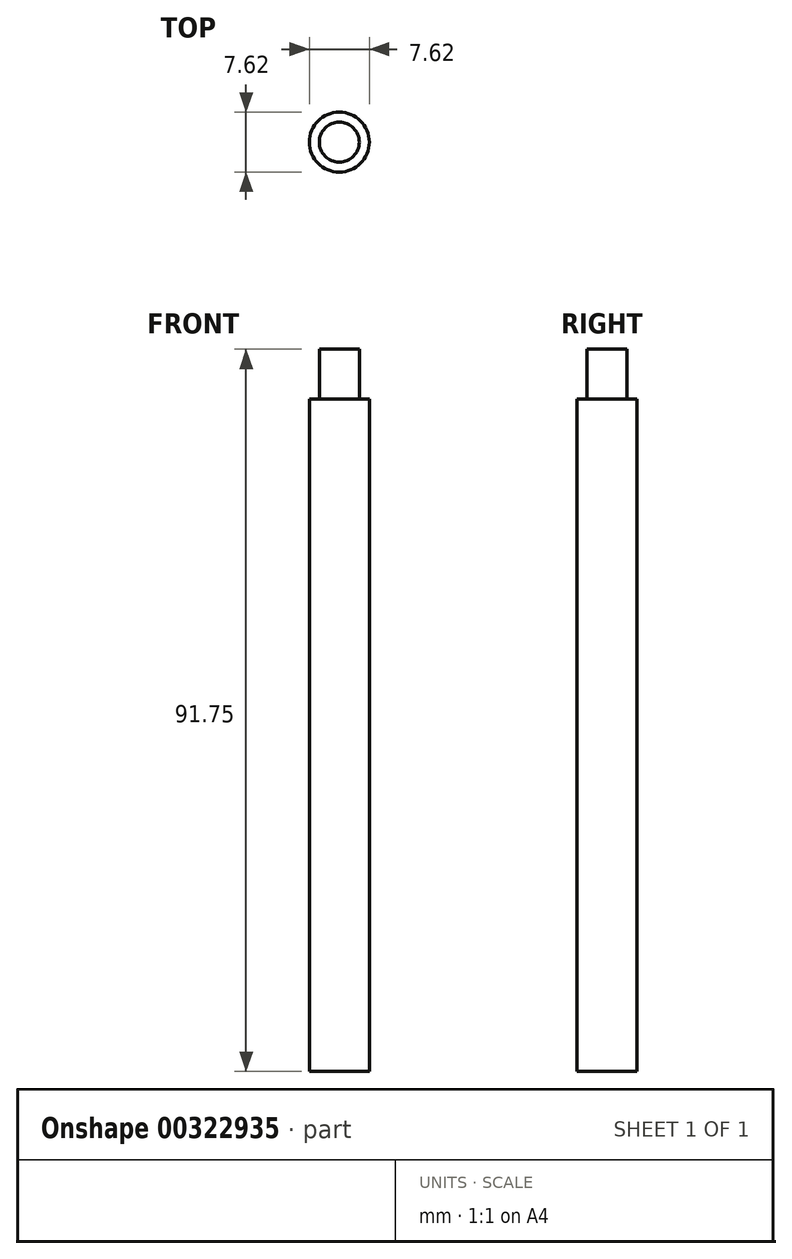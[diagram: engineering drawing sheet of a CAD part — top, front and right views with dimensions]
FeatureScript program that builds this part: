
annotation { "Feature Type Name" : "Feature", "Feature Type Description" : "" }
export const myFeature = defineFeature(function(context is Context, id is Id, definition is map)
    precondition{}
    {
        {
            var Q0;
            Q0=qCreatedBy(makeId("Top.planeOp"),FACE);
            var sketch = newSketch(context, id + "F0", { "sketchPlane" : qUnion([Q0])});
            skCircle(sketch, "E0", {"center": v(0, 0) * mm, "radius": 3.81 * mm});
            skSolve(sketch);
        }
        {
            var Q0;
            Q0=makeQuery(id+"F0.imprint","IMPRINT",FACE,{"disambiguationData":[TD([[makeQuery(id+"F0.imprint","IMPRINT",EDGE,{"derivedFrom":sQuery(id+"F0.wireOp",EDGE,"E0")}),1.0]])]});
            extrude(context, id + "F1", {"entities" : qUnion([Q0]), "depth" : 60 * mm, "hasSecondDirection" : true, "secondDirectionOppositeDirection" : true, "secondDirectionDepth" : 25.4 * mm});
        }
        {
            var Q0;
            Q0=makeQuery(id+"F1.opExtrude","CAP_FACE",FACE,{"disambiguationData":[OSD([sQuery(id+"F0.wireOp",EDGE,"E0")])],"isStart":false});
            var sketch = newSketch(context, id + "F2", { "sketchPlane" : qUnion([Q0])});
            skCircle(sketch, "E1", {"center": v(0, 0) * mm, "radius": 2.54 * mm});
            skSolve(sketch);
        }
        {
            var Q0;
            Q0 = qSketchRegion(id + "F2", true);
            extrude(context, id + "F3", {"entities" : qUnion([Q0]), "operationType" : NewBodyOperationType.ADD, "depth" : 6.35 * mm});
        }
    });
